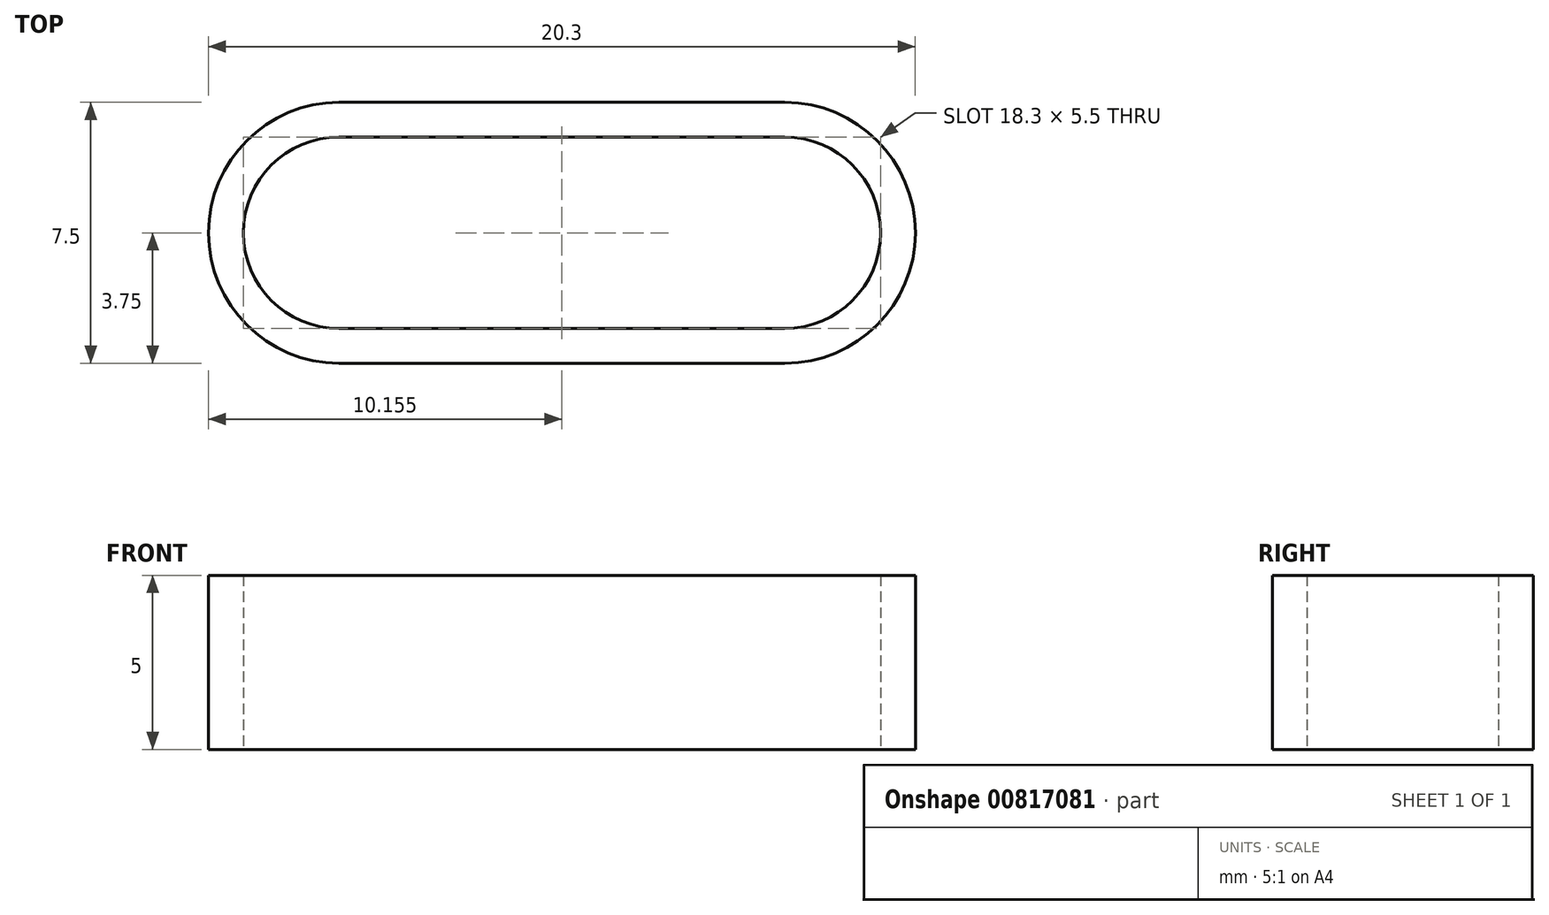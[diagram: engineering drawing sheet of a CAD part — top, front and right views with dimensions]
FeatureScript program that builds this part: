
annotation { "Feature Type Name" : "Feature", "Feature Type Description" : "" }
export const myFeature = defineFeature(function(context is Context, id is Id, definition is map)
    precondition{}
    {
        {
            var Q0;
            Q0=qCreatedBy(makeId("Top.planeOp"),FACE);
            var sketch = newSketch(context, id + "F0", { "sketchPlane" : qUnion([Q0])});
            skLineSegment(sketch, "E0", {"start": v(-7.36, 2.75) * mm, "end": v(5.44, 2.75) * mm});
            skLineSegment(sketch, "E1", {"start": v(-7.36, -2.75) * mm, "end": v(5.44, -2.75) * mm});
            skCircle(sketch, "E2", {"center": v(5.44, 0) * mm, "radius": 2.75 * mm});
            skPoint(sketch, "E2.third.point", {"position": v(8.2, 0) * mm});
            skCircle(sketch, "E3", {"center": v(-7.36, 0) * mm, "radius": 2.75 * mm});
            skPoint(sketch, "E3.third.point", {"position": v(-4.6, 0) * mm});
            skCircle(sketch, "E4.0", {"center": v(-7.36, 0) * mm, "radius": 3.75 * mm});
            skLineSegment(sketch, "E5.0", {"start": v(-7.67, 3.75) * mm, "end": v(8.05, 3.75) * mm});
            skLineSegment(sketch, "E6.0", {"start": v(-7.67, -3.75) * mm, "end": v(8.05, -3.75) * mm});
            skCircle(sketch, "E7.0", {"center": v(5.44, 0) * mm, "radius": 3.75 * mm});
            skLineSegment(sketch, "E8", {"start": v(-10.1, 0) * mm, "end": v(8.2, 0) * mm});
            skSolve(sketch);
        }
        {
            var Q0;
            {var subQ0=sQuery(id+"F0.wireOp",EDGE,"E4.0");var subQ1=sQuery(id+"F0.wireOp",EDGE,"E0");var subQ2=makeQuery(id+"F0.imprint","INTERSECT",VERTEX,{"derivedFrom":[subQ1,subQ0]});Q0=makeQuery(id+"F0.imprint","IMPRINT",FACE,{"disambiguationData":[TD([[makeQuery(id+"F0.imprint","IMPRINT",EDGE,{"disambiguationData":[TD([[subQ2,-1.0]])],"derivedFrom":subQ1}),1.0]])]});}
            var Q1;
            {var subQ0=sQuery(id+"F0.wireOp",EDGE,"E3");var subQ1=sQuery(id+"F0.wireOp",EDGE,"E0");var subQ5=makeQuery(id+"F0.imprint","INTERSECT",VERTEX,{"disambiguationData":[OD(1.0)],"derivedFrom":[subQ1,subQ0]});Q1=makeQuery(id+"F0.imprint","IMPRINT",FACE,{"disambiguationData":[TD([[makeQuery(id+"F0.imprint","IMPRINT",EDGE,{"disambiguationData":[TD([[subQ5,-1.0]])],"derivedFrom":subQ1}),1.0]])]});}
            var Q2;
            {var subQ0=sQuery(id+"F0.wireOp",EDGE,"E4.0");var subQ1=sQuery(id+"F0.wireOp",EDGE,"E1");var subQ2=makeQuery(id+"F0.imprint","INTERSECT",VERTEX,{"derivedFrom":[subQ1,subQ0]});Q2=makeQuery(id+"F0.imprint","IMPRINT",FACE,{"disambiguationData":[TD([[makeQuery(id+"F0.imprint","IMPRINT",EDGE,{"disambiguationData":[TD([[subQ2,-1.0]])],"derivedFrom":subQ1}),-1.0]])]});}
            var Q3;
            {var subQ4=sQuery(id+"F0.wireOp",EDGE,"E0");var subQ7=sQuery(id+"F0.wireOp",EDGE,"E7.0");var subQ9=makeQuery(id+"F0.imprint","INTERSECT",VERTEX,{"derivedFrom":[subQ4,subQ7]});Q3=makeQuery(id+"F0.imprint","IMPRINT",FACE,{"disambiguationData":[TD([[makeQuery(id+"F0.imprint","IMPRINT",EDGE,{"disambiguationData":[TD([[subQ9,-1.0]])],"derivedFrom":subQ4}),1.0]])]});}
            extrude(context, id + "F1", {"entities" : qUnion([Q0, Q1, Q2, Q3]), "depth" : 5 * mm, "offsetDistance" : 25 * mm});
        }
    });
